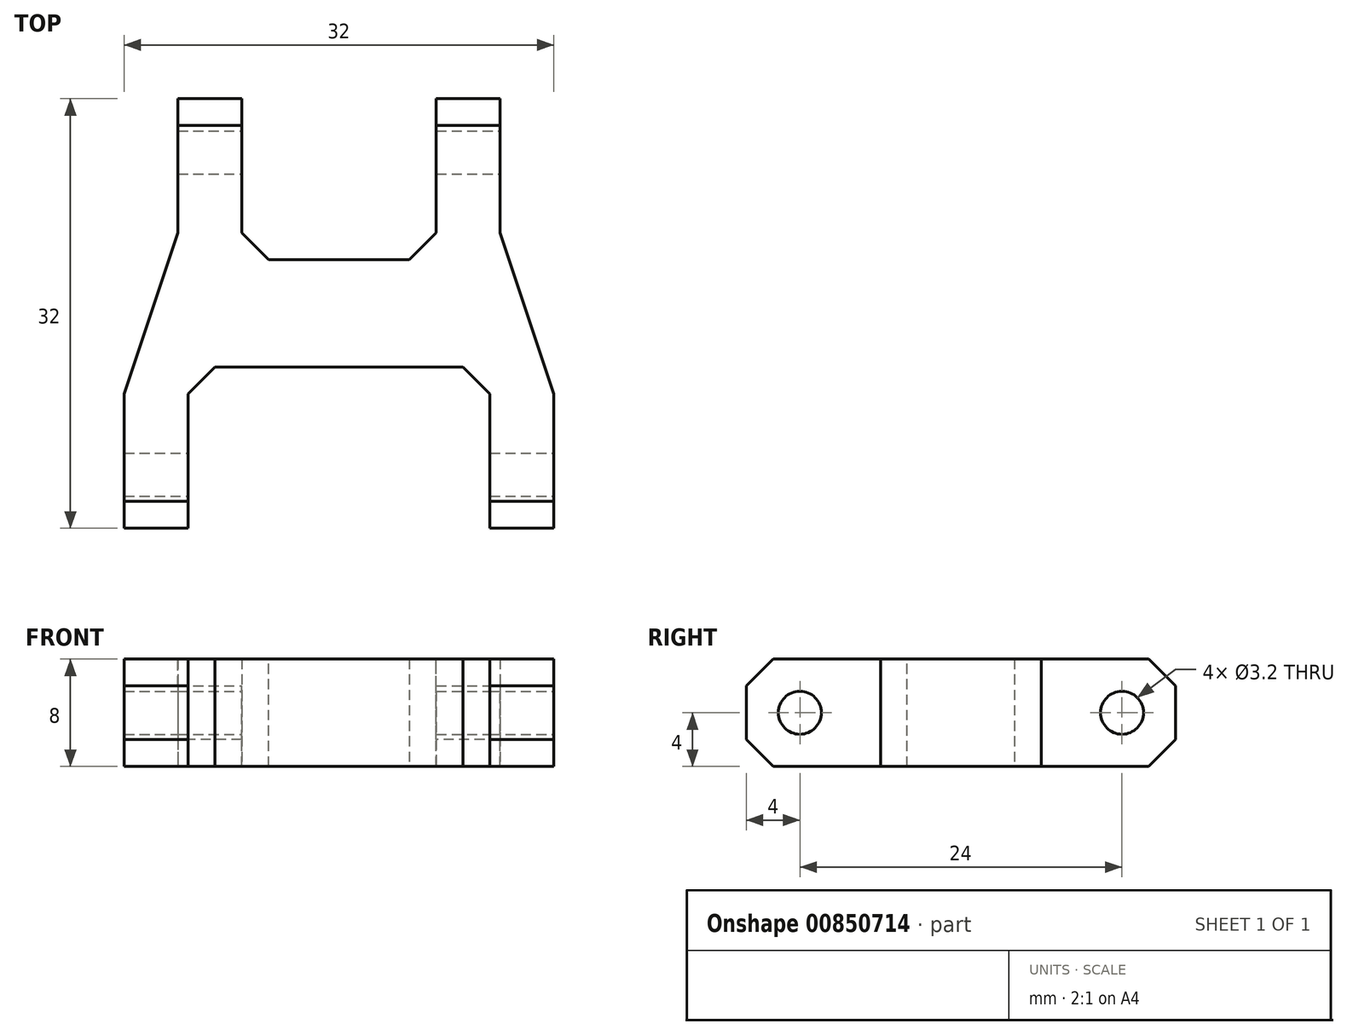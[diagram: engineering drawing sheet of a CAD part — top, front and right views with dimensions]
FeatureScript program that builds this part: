
annotation { "Feature Type Name" : "Feature", "Feature Type Description" : "" }
export const myFeature = defineFeature(function(context is Context, id is Id, definition is map)
    precondition{}
    {
        {
            var Q0;
            Q0=qCreatedBy(makeId("Top.planeOp"),FACE);
            var sketch = newSketch(context, id + "F0", { "sketchPlane" : qUnion([Q0])});
            skLineSegment(sketch, "E0", {"start": v(-12, 22) * mm, "end": v(12, 22) * mm});
            skLineSegment(sketch, "E1", {"start": v(12, 22) * mm, "end": v(12, 12) * mm});
            skLineSegment(sketch, "E2", {"start": v(12, 12) * mm, "end": v(16, 0) * mm});
            skLineSegment(sketch, "E3", {"start": v(16, 0) * mm, "end": v(16, -10) * mm});
            skLineSegment(sketch, "E4", {"start": v(16, -10) * mm, "end": v(-16, -10) * mm});
            skLineSegment(sketch, "E5", {"start": v(-12, 12) * mm, "end": v(-12, 22) * mm});
            skLineSegment(sketch, "E6", {"start": v(-16, -10) * mm, "end": v(-16, 0) * mm});
            skLineSegment(sketch, "E7", {"start": v(-16, 0) * mm, "end": v(-12, 12) * mm});
            skSolve(sketch);
        }
        {
            var Q0;
            Q0 = qSketchRegion(id + "F0", true);
            extrude(context, id + "F1", {"entities" : qUnion([Q0]), "depth" : 8 * mm, "offsetDistance" : 25 * mm});
        }
        {
            var Q0;
            Q0=makeQuery(id+"F1.opExtrude","CAP_FACE",FACE,{"disambiguationData":[OSD([sQuery(id+"F0.wireOp",EDGE,"E0"),sQuery(id+"F0.wireOp",EDGE,"E1"),sQuery(id+"F0.wireOp",EDGE,"E2"),sQuery(id+"F0.wireOp",EDGE,"E3"),sQuery(id+"F0.wireOp",EDGE,"E4"),sQuery(id+"F0.wireOp",EDGE,"E5"),sQuery(id+"F0.wireOp",EDGE,"E6"),sQuery(id+"F0.wireOp",EDGE,"E7")])],"isStart":false});
            var sketch = newSketch(context, id + "F2", { "sketchPlane" : qUnion([Q0])});
            skLineSegment(sketch, "E8.bottom", {"start": v(-7.25, 22) * mm, "end": v(7.25, 22) * mm});
            skLineSegment(sketch, "E8.top", {"start": v(-7.25, 10) * mm, "end": v(7.25, 10) * mm});
            skLineSegment(sketch, "E8.left", {"start": v(-7.25, 22) * mm, "end": v(-7.25, 10) * mm});
            skLineSegment(sketch, "E8.right", {"start": v(7.25, 22) * mm, "end": v(7.25, 10) * mm});
            skLineSegment(sketch, "E9.bottom", {"start": v(-11.25, -10) * mm, "end": v(11.25, -10) * mm});
            skLineSegment(sketch, "E9.top", {"start": v(-11.25, 2) * mm, "end": v(11.25, 2) * mm});
            skLineSegment(sketch, "E9.left", {"start": v(-11.25, -10) * mm, "end": v(-11.25, 2) * mm});
            skLineSegment(sketch, "E9.right", {"start": v(11.25, -10) * mm, "end": v(11.25, 2) * mm});
            skSolve(sketch);
        }
        {
            var Q0;
            Q0 = qSketchRegion(id + "F2", true);
            extrude(context, id + "F3", {"entities" : qUnion([Q0]), "operationType" : NewBodyOperationType.REMOVE, "endBound" : BoundingType.UP_TO_NEXT, "oppositeDirection" : true, "depth" : 25 * mm, "offsetDistance" : 25 * mm});
        }
        {
            var Q0;
            Q0=makeQuery(id+"F1.opExtrude","SWEPT_FACE",FACE,{"disambiguationData":[OSD([sQuery(id+"F0.wireOp",EDGE,"E3")])]});
            var sketch = newSketch(context, id + "F4", { "sketchPlane" : qUnion([Q0])});
            skCircle(sketch, "E10", {"center": v(-6, 4) * mm, "radius": 1.6 * mm});
            skLineSegment(sketch, "E11", {"start": v(-10, 0) * mm, "end": v(-2, 8) * mm, "construction": true});
            skLineSegment(sketch, "E12", {"start": v(-2, 8) * mm, "end": v(-10, 8) * mm, "construction": true});
            skSolve(sketch);
        }
        {
            var Q0;
            Q0 = qSketchRegion(id + "F4", true);
            var Q1;
            Q1=makeQuery(id+"F1.opExtrude","SWEPT_FACE",FACE,{"disambiguationData":[OSD([sQuery(id+"F0.wireOp",EDGE,"E6")])]});
            extrude(context, id + "F5", {"entities" : qUnion([Q0]), "operationType" : NewBodyOperationType.REMOVE, "endBound" : BoundingType.UP_TO_SURFACE, "oppositeDirection" : true, "depth" : 25 * mm, "endBoundEntityFace" : qUnion([Q1]), "offsetDistance" : 25 * mm});
        }
        {
            var Q0;
            Q0=makeQuery(id+"F1.opExtrude","SWEPT_FACE",FACE,{"disambiguationData":[OSD([sQuery(id+"F0.wireOp",EDGE,"E1")])]});
            var sketch = newSketch(context, id + "F6", { "sketchPlane" : qUnion([Q0])});
            skCircle(sketch, "E13", {"center": v(18, 4) * mm, "radius": 1.6 * mm});
            skLineSegment(sketch, "E14", {"start": v(22, 8) * mm, "end": v(14, 0) * mm, "construction": true});
            skLineSegment(sketch, "E15", {"start": v(14, 0) * mm, "end": v(22, 0) * mm, "construction": true});
            skSolve(sketch);
        }
        {
            var Q0;
            Q0 = qSketchRegion(id + "F6", true);
            var Q1;
            Q1=makeQuery(id+"F1.opExtrude","SWEPT_FACE",FACE,{"disambiguationData":[OSD([sQuery(id+"F0.wireOp",EDGE,"E5")])]});
            extrude(context, id + "F7", {"entities" : qUnion([Q0]), "operationType" : NewBodyOperationType.REMOVE, "endBound" : BoundingType.UP_TO_SURFACE, "oppositeDirection" : true, "depth" : 25 * mm, "endBoundEntityFace" : qUnion([Q1]), "offsetDistance" : 25 * mm});
        }
        {
            var Q0;
            Q0=makeQuery(id+"F3.boolean.opBoolean","COPY",EDGE,{"derivedFrom":makeQuery(id+"F3.opExtrude","SWEPT_EDGE",EDGE,{"disambiguationData":[OSD([sQuery(id+"F2.wireOp",EDGE,"E9.top"),sQuery(id+"F2.wireOp",EDGE,"E9.left")])]})});
            var Q1;
            Q1=makeQuery(id+"F3.boolean.opBoolean","COPY",EDGE,{"derivedFrom":makeQuery(id+"F3.opExtrude","SWEPT_EDGE",EDGE,{"disambiguationData":[OSD([sQuery(id+"F2.wireOp",EDGE,"E9.top"),sQuery(id+"F2.wireOp",EDGE,"E9.right")])]})});
            var Q2;
            Q2=makeQuery(id+"F3.boolean.opBoolean","COPY",EDGE,{"derivedFrom":makeQuery(id+"F3.opExtrude","SWEPT_EDGE",EDGE,{"disambiguationData":[OSD([sQuery(id+"F2.wireOp",EDGE,"E8.top"),sQuery(id+"F2.wireOp",EDGE,"E8.left")])]})});
            var Q3;
            Q3=makeQuery(id+"F3.boolean.opBoolean","COPY",EDGE,{"derivedFrom":makeQuery(id+"F3.opExtrude","SWEPT_EDGE",EDGE,{"disambiguationData":[OSD([sQuery(id+"F2.wireOp",EDGE,"E8.top"),sQuery(id+"F2.wireOp",EDGE,"E8.right")])]})});
            chamfer(context, id + "F8", {"entities" : qUnion([Q0, Q1, Q2, Q3]), "width" : 2 * mm, "tangentPropagation" : true});
        }
        {
            var Q0;
            {var subQ0=sQuery(id+"F0.wireOp",EDGE,"E6");var subQ1=sQuery(id+"F0.wireOp",EDGE,"E4");Q0=makeQuery(id+"F3.boolean.opBoolean","SPLIT",EDGE,{"disambiguationData":[TD([makeQuery(id+"F1.opExtrude","SWEPT_FACE",FACE,{"disambiguationData":[OSD([subQ0])]})])],"derivedFrom":makeQuery(id+"F1.opExtrude","CAP_EDGE",EDGE,{"disambiguationData":[OSD([subQ1])],"isStart":false})});}
            var Q1;
            {var subQ0=sQuery(id+"F0.wireOp",EDGE,"E6");var subQ1=sQuery(id+"F0.wireOp",EDGE,"E4");Q1=makeQuery(id+"F3.boolean.opBoolean","SPLIT",EDGE,{"disambiguationData":[TD([makeQuery(id+"F1.opExtrude","SWEPT_FACE",FACE,{"disambiguationData":[OSD([subQ0])]})])],"derivedFrom":makeQuery(id+"F1.opExtrude","CAP_EDGE",EDGE,{"disambiguationData":[OSD([subQ1])],"isStart":true})});}
            var Q2;
            Q2=makeQuery(id+"F3.boolean.opBoolean","COPY",EDGE,{"derivedFrom":makeQuery(id+"F3.opExtrude","CAP_EDGE",EDGE,{"disambiguationData":[OSD([sQuery(id+"F2.wireOp",EDGE,"E9.top")])],"isStart":true})});
            var Q3;
            Q3=makeQuery(id+"F3.boolean.opBoolean","COPY",EDGE,{"derivedFrom":makeQuery(id+"F3.opExtrude","TWEAK_EDGE",EDGE,{"derivedFrom":[makeQuery(id+"F1.opExtrude","CAP_FACE",FACE,{"disambiguationData":[OSD([sQuery(id+"F0.wireOp",EDGE,"E0"),sQuery(id+"F0.wireOp",EDGE,"E1"),sQuery(id+"F0.wireOp",EDGE,"E2"),sQuery(id+"F0.wireOp",EDGE,"E3"),sQuery(id+"F0.wireOp",EDGE,"E4"),sQuery(id+"F0.wireOp",EDGE,"E5"),sQuery(id+"F0.wireOp",EDGE,"E6"),sQuery(id+"F0.wireOp",EDGE,"E7")])],"isStart":true}),makeQuery(id+"F2.imprint","IMPRINT",EDGE,{"derivedFrom":sQuery(id+"F2.wireOp",EDGE,"E9.top")})]})});
            var Q4;
            {var subQ0=sQuery(id+"F0.wireOp",EDGE,"E4");var subQ1=sQuery(id+"F0.wireOp",EDGE,"E3");Q4=makeQuery(id+"F3.boolean.opBoolean","SPLIT",EDGE,{"disambiguationData":[TD([makeQuery(id+"F1.opExtrude","SWEPT_FACE",FACE,{"disambiguationData":[OSD([subQ1])]})])],"derivedFrom":makeQuery(id+"F1.opExtrude","CAP_EDGE",EDGE,{"disambiguationData":[OSD([subQ0])],"isStart":false})});}
            var Q5;
            {var subQ0=sQuery(id+"F0.wireOp",EDGE,"E4");var subQ1=sQuery(id+"F0.wireOp",EDGE,"E3");Q5=makeQuery(id+"F3.boolean.opBoolean","SPLIT",EDGE,{"disambiguationData":[TD([makeQuery(id+"F1.opExtrude","SWEPT_FACE",FACE,{"disambiguationData":[OSD([subQ1])]})])],"derivedFrom":makeQuery(id+"F1.opExtrude","CAP_EDGE",EDGE,{"disambiguationData":[OSD([subQ0])],"isStart":true})});}
            var Q6;
            {var subQ0=sQuery(id+"F0.wireOp",EDGE,"E0");var subQ1=sQuery(id+"F0.wireOp",EDGE,"E1");Q6=makeQuery(id+"F3.boolean.opBoolean","SPLIT",EDGE,{"disambiguationData":[TD([makeQuery(id+"F1.opExtrude","SWEPT_FACE",FACE,{"disambiguationData":[OSD([subQ1])]})])],"derivedFrom":makeQuery(id+"F1.opExtrude","CAP_EDGE",EDGE,{"disambiguationData":[OSD([subQ0])],"isStart":false})});}
            var Q7;
            Q7=makeQuery(id+"F3.boolean.opBoolean","COPY",EDGE,{"derivedFrom":makeQuery(id+"F3.opExtrude","CAP_EDGE",EDGE,{"disambiguationData":[OSD([sQuery(id+"F2.wireOp",EDGE,"E8.top")])],"isStart":true})});
            var Q8;
            Q8=makeQuery(id+"F3.boolean.opBoolean","COPY",EDGE,{"derivedFrom":makeQuery(id+"F3.opExtrude","TWEAK_EDGE",EDGE,{"derivedFrom":[makeQuery(id+"F1.opExtrude","CAP_FACE",FACE,{"disambiguationData":[OSD([sQuery(id+"F0.wireOp",EDGE,"E0"),sQuery(id+"F0.wireOp",EDGE,"E1"),sQuery(id+"F0.wireOp",EDGE,"E2"),sQuery(id+"F0.wireOp",EDGE,"E3"),sQuery(id+"F0.wireOp",EDGE,"E4"),sQuery(id+"F0.wireOp",EDGE,"E5"),sQuery(id+"F0.wireOp",EDGE,"E6"),sQuery(id+"F0.wireOp",EDGE,"E7")])],"isStart":true}),makeQuery(id+"F2.imprint","IMPRINT",EDGE,{"derivedFrom":sQuery(id+"F2.wireOp",EDGE,"E8.top")})]})});
            var Q9;
            {var subQ0=sQuery(id+"F0.wireOp",EDGE,"E0");var subQ1=sQuery(id+"F0.wireOp",EDGE,"E5");Q9=makeQuery(id+"F3.boolean.opBoolean","SPLIT",EDGE,{"disambiguationData":[TD([makeQuery(id+"F1.opExtrude","SWEPT_FACE",FACE,{"disambiguationData":[OSD([subQ1])]})])],"derivedFrom":makeQuery(id+"F1.opExtrude","CAP_EDGE",EDGE,{"disambiguationData":[OSD([subQ0])],"isStart":false})});}
            var Q10;
            {var subQ0=sQuery(id+"F0.wireOp",EDGE,"E0");var subQ1=sQuery(id+"F0.wireOp",EDGE,"E5");Q10=makeQuery(id+"F3.boolean.opBoolean","SPLIT",EDGE,{"disambiguationData":[TD([makeQuery(id+"F1.opExtrude","SWEPT_FACE",FACE,{"disambiguationData":[OSD([subQ1])]})])],"derivedFrom":makeQuery(id+"F1.opExtrude","CAP_EDGE",EDGE,{"disambiguationData":[OSD([subQ0])],"isStart":true})});}
            var Q11;
            {var subQ0=sQuery(id+"F0.wireOp",EDGE,"E0");var subQ1=sQuery(id+"F0.wireOp",EDGE,"E1");Q11=makeQuery(id+"F3.boolean.opBoolean","SPLIT",EDGE,{"disambiguationData":[TD([makeQuery(id+"F1.opExtrude","SWEPT_FACE",FACE,{"disambiguationData":[OSD([subQ1])]})])],"derivedFrom":makeQuery(id+"F1.opExtrude","CAP_EDGE",EDGE,{"disambiguationData":[OSD([subQ0])],"isStart":true})});}
            chamfer(context, id + "F9", {"entities" : qUnion([Q0, Q1, Q2, Q3, Q4, Q5, Q6, Q7, Q8, Q9, Q10, Q11]), "width" : 2 * mm, "tangentPropagation" : true});
        }
    });
